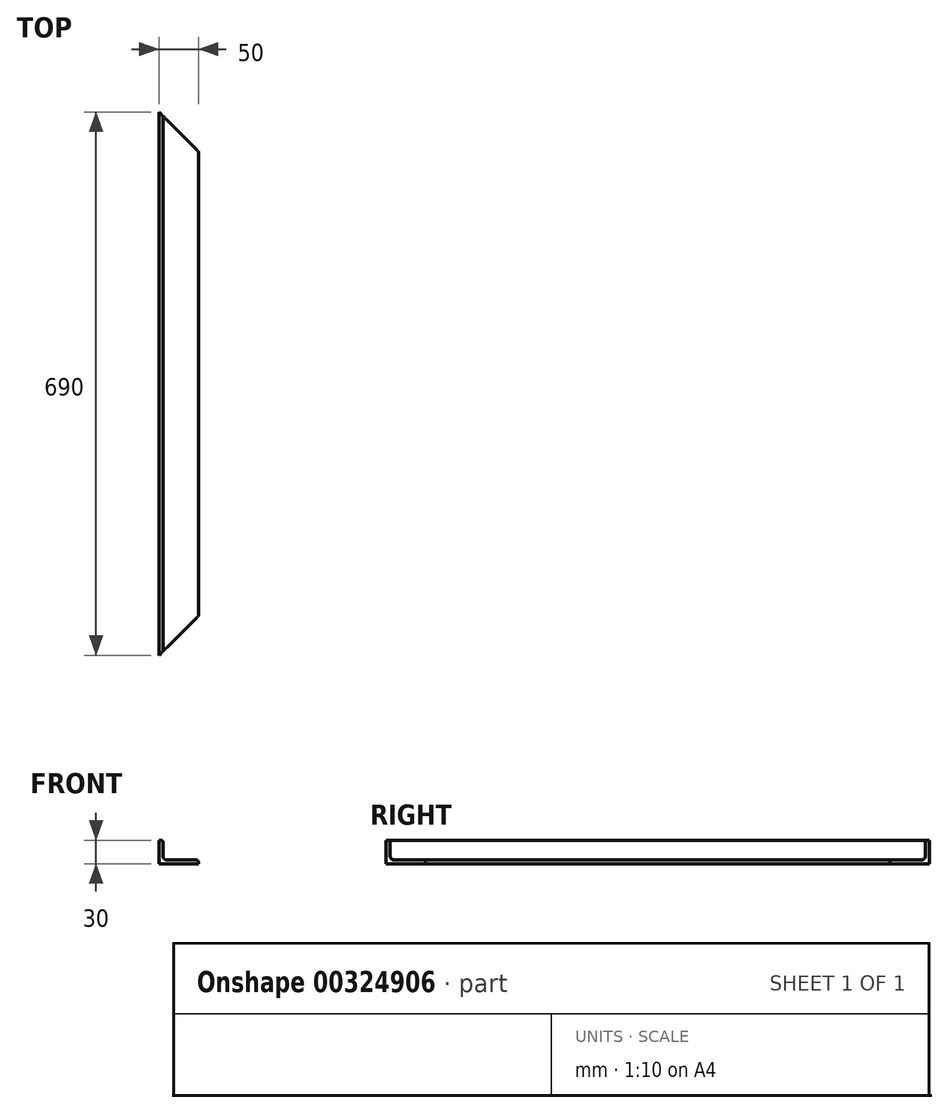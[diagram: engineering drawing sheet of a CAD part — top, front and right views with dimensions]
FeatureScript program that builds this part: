
annotation { "Feature Type Name" : "Feature", "Feature Type Description" : "" }
export const myFeature = defineFeature(function(context is Context, id is Id, definition is map)
    precondition{}
    {
        {
            var Q0;
            Q0=qCreatedBy(makeId("Front.planeOp"),FACE);
            var sketch = newSketch(context, id + "F0", { "sketchPlane" : qUnion([Q0])});
            skLineSegment(sketch, "E0.bottom", {"start": v(0, 0) * mm, "end": v(5, 0) * mm});
            skLineSegment(sketch, "E0.top", {"start": v(0, 30) * mm, "end": v(2.5, 30) * mm});
            skLineSegment(sketch, "E0.left", {"start": v(0, 0) * mm, "end": v(0, 30) * mm});
            skLineSegment(sketch, "E0.right", {"start": v(5, 10) * mm, "end": v(5, 27.5) * mm});
            skLineSegment(sketch, "E1.bottom", {"start": v(0, 0) * mm, "end": v(50, 0) * mm});
            skLineSegment(sketch, "E1.top", {"start": v(10, 5) * mm, "end": v(47.5, 5) * mm});
            skLineSegment(sketch, "E1.left", {"start": v(0, 0) * mm, "end": v(0, 5) * mm});
            skLineSegment(sketch, "E1.right", {"start": v(50, 0) * mm, "end": v(50, 2.5) * mm});
            skPoint(sketch, "E2.visualSharp", {"position": v(5, 30) * mm});
            skArc(sketch, "E2.filletArc", {"start": v(5, 27.5) * mm, "mid": v(4.27, 29.27) * mm, "end": v(2.5, 30) * mm});
            skPoint(sketch, "E3.visualSharp", {"position": v(50, 5) * mm});
            skArc(sketch, "E3.filletArc", {"start": v(50, 2.5) * mm, "mid": v(49.27, 4.27) * mm, "end": v(47.5, 5) * mm});
            skPoint(sketch, "E4.visualSharp", {"position": v(5, 5) * mm});
            skArc(sketch, "E4.filletArc", {"start": v(5, 10) * mm, "mid": v(6.46, 6.46) * mm, "end": v(10, 5) * mm});
            skSolve(sketch);
        }
        {
            var Q0;
            Q0=makeQuery(id+"F0.imprint","IMPRINT",FACE,{"disambiguationData":[TD([[makeQuery(id+"F0.imprint","IMPRINT",EDGE,{"derivedFrom":sQuery(id+"F0.wireOp",EDGE,"E0.top")}),-1.0]])]});
            extrude(context, id + "F1", {"entities" : qUnion([Q0]), "oppositeDirection" : true, "depth" : 690 * mm});
        }
        {
            var Q0;
            Q0=makeQuery(id+"F1.opExtrude","SWEPT_FACE",FACE,{"disambiguationData":[OSD([sQuery(id+"F0.wireOp",EDGE,"E0.top")])]});
            var sketch = newSketch(context, id + "F2", { "sketchPlane" : qUnion([Q0])});
            skLineSegment(sketch, "E5", {"start": v(-62.59, 345) * mm, "end": v(124.15, 345) * mm, "construction": true});
            skLineSegment(sketch, "E6", {"start": v(0, 0) * mm, "end": v(56.9, 0) * mm});
            skLineSegment(sketch, "E7", {"start": v(56.9, 0) * mm, "end": v(56.9, 56.9) * mm});
            skLineSegment(sketch, "E8", {"start": v(56.9, 56.9) * mm, "end": v(0, 0) * mm});
            skLineSegment(sketch, "E9.MirrorCS", {"start": v(56.9, 633.1) * mm, "end": v(0, 690) * mm});
            skLineSegment(sketch, "E10.MirrorCS", {"start": v(56.9, 690) * mm, "end": v(56.9, 633.1) * mm});
            skLineSegment(sketch, "E11.MirrorCS", {"start": v(0, 690) * mm, "end": v(56.9, 690) * mm});
            skSolve(sketch);
        }
        {
            var Q0;
            {var subQ3=sQuery(id+"F2.wireOp",EDGE,"E7");Q0=makeQuery(id+"F2.imprint","IMPRINT",FACE,{"disambiguationData":[TD([[makeQuery(id+"F2.imprint","IMPRINT",EDGE,{"derivedFrom":subQ3}),1.0]])]});}
            var Q1;
            {var subQ0=sQuery(id+"F2.wireOp",EDGE,"E10.MirrorCS");Q1=makeQuery(id+"F2.imprint","IMPRINT",FACE,{"disambiguationData":[TD([[makeQuery(id+"F2.imprint","IMPRINT",EDGE,{"derivedFrom":subQ0}),-1.0]])]});}
            var Q2;
            {var subQ1=sQuery(id+"F2.wireOp",EDGE,"E9.MirrorCS");var subQ2=sQuery(id+"F0.wireOp",EDGE,"E0.top");var subQ4=makeQuery(id+"F1.opExtrude","SWEPT_EDGE",EDGE,{"disambiguationData":[OSD([subQ2,sQuery(id+"F0.wireOp",EDGE,"E2.filletArc")])]});var subQ5=makeQuery(id+"F2.imprint","INTERSECT",VERTEX,{"derivedFrom":[subQ4,subQ1]});Q2=makeQuery(id+"F2.imprint","IMPRINT",FACE,{"disambiguationData":[TD([[makeQuery(id+"F2.imprint","IMPRINT",EDGE,{"disambiguationData":[TD([[subQ5,-1.0]])],"derivedFrom":subQ1}),-1.0]])]});}
            var Q3;
            {var subQ1=sQuery(id+"F2.wireOp",EDGE,"E6");var subQ2=sQuery(id+"F0.wireOp",EDGE,"E0.top");var subQ4=makeQuery(id+"F1.opExtrude","SWEPT_EDGE",EDGE,{"disambiguationData":[OSD([subQ2,sQuery(id+"F0.wireOp",EDGE,"E2.filletArc")])]});var subQ5=makeQuery(id+"F2.imprint","INTERSECT",VERTEX,{"derivedFrom":[subQ4,subQ1]});Q3=makeQuery(id+"F2.imprint","IMPRINT",FACE,{"disambiguationData":[TD([[makeQuery(id+"F2.imprint","IMPRINT",EDGE,{"disambiguationData":[TD([[subQ5,1.0]])],"derivedFrom":subQ1}),1.0]])]});}
            extrude(context, id + "F3", {"entities" : qUnion([Q0, Q1, Q2, Q3]), "operationType" : NewBodyOperationType.REMOVE, "endBound" : BoundingType.THROUGH_ALL, "oppositeDirection" : true, "depth" : 25 * mm});
        }
    });
